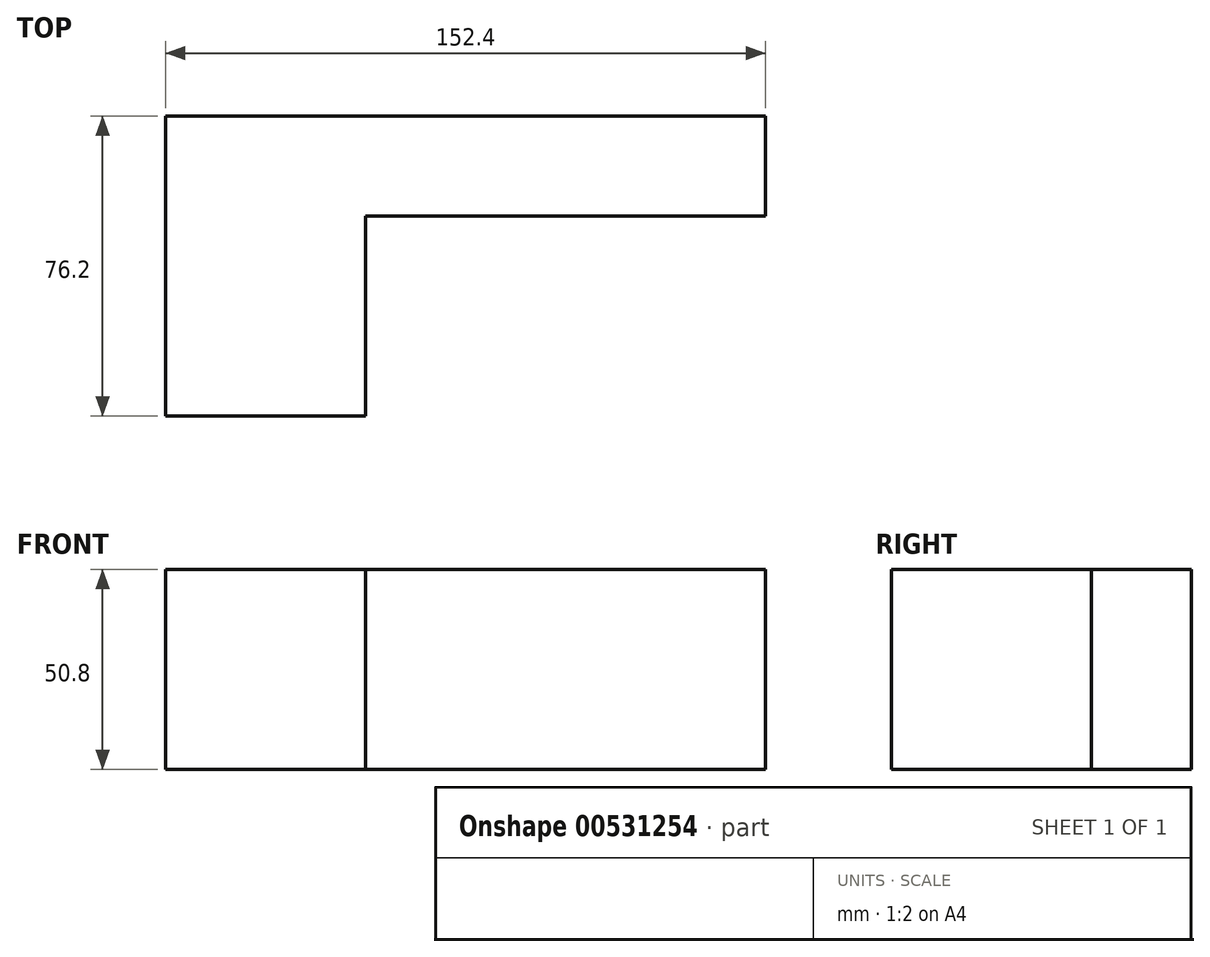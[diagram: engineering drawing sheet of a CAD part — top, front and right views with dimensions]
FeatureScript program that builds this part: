
annotation { "Feature Type Name" : "Feature", "Feature Type Description" : "" }
export const myFeature = defineFeature(function(context is Context, id is Id, definition is map)
    precondition{}
    {
        {
            var Q0;
            Q0=qCreatedBy(makeId("Top.planeOp"),FACE);
            var sketch = newSketch(context, id + "F0", { "sketchPlane" : qUnion([Q0])});
            skLineSegment(sketch, "E0", {"start": v(-88.88, 69.3) * mm, "end": v(-88.88, -6.9) * mm});
            skLineSegment(sketch, "E1", {"start": v(-88.88, -6.9) * mm, "end": v(-38.08, -6.9) * mm});
            skLineSegment(sketch, "E2", {"start": v(-38.08, -6.9) * mm, "end": v(-38.08, 43.9) * mm});
            skLineSegment(sketch, "E3", {"start": v(-38.08, 43.9) * mm, "end": v(63.52, 43.9) * mm});
            skLineSegment(sketch, "E4", {"start": v(63.52, 43.9) * mm, "end": v(63.52, 69.3) * mm});
            skLineSegment(sketch, "E5", {"start": v(63.52, 69.3) * mm, "end": v(-88.88, 69.3) * mm});
            skLineSegment(sketch, "E6.bottom", {"start": v(23.8, 69.3) * mm, "end": v(63.52, 69.3) * mm});
            skLineSegment(sketch, "E6.top", {"start": v(23.8, 43.9) * mm, "end": v(63.52, 43.9) * mm});
            skLineSegment(sketch, "E6.left", {"start": v(23.8, 69.3) * mm, "end": v(23.8, 43.9) * mm});
            skLineSegment(sketch, "E6.right", {"start": v(63.52, 69.3) * mm, "end": v(63.52, 43.9) * mm});
            skSolve(sketch);
        }
        {
            var Q0;
            Q0 = qSketchRegion(id + "F0", true);
            extrude(context, id + "F1", {"entities" : qUnion([Q0]), "depth" : 25.4 * mm, "offsetDistance" : 25.4 * mm});
        }
        {
            var Q0;
            Q0=makeQuery(id+"F1.opExtrude","CAP_FACE",FACE,{"disambiguationData":[OSD([sQuery(id+"F0.wireOp",EDGE,"E0"),sQuery(id+"F0.wireOp",EDGE,"E1"),sQuery(id+"F0.wireOp",EDGE,"E2"),sQuery(id+"F0.wireOp",EDGE,"E3"),sQuery(id+"F0.wireOp",EDGE,"E5"),sQuery(id+"F0.wireOp",EDGE,"E6.bottom"),sQuery(id+"F0.wireOp",EDGE,"E6.top"),sQuery(id+"F0.wireOp",EDGE,"E6.right")])],"isStart":false});
            extrude(context, id + "F2", {"entities" : qUnion([Q0]), "operationType" : NewBodyOperationType.ADD, "depth" : 25.4 * mm, "offsetDistance" : 25.4 * mm});
        }
    });
